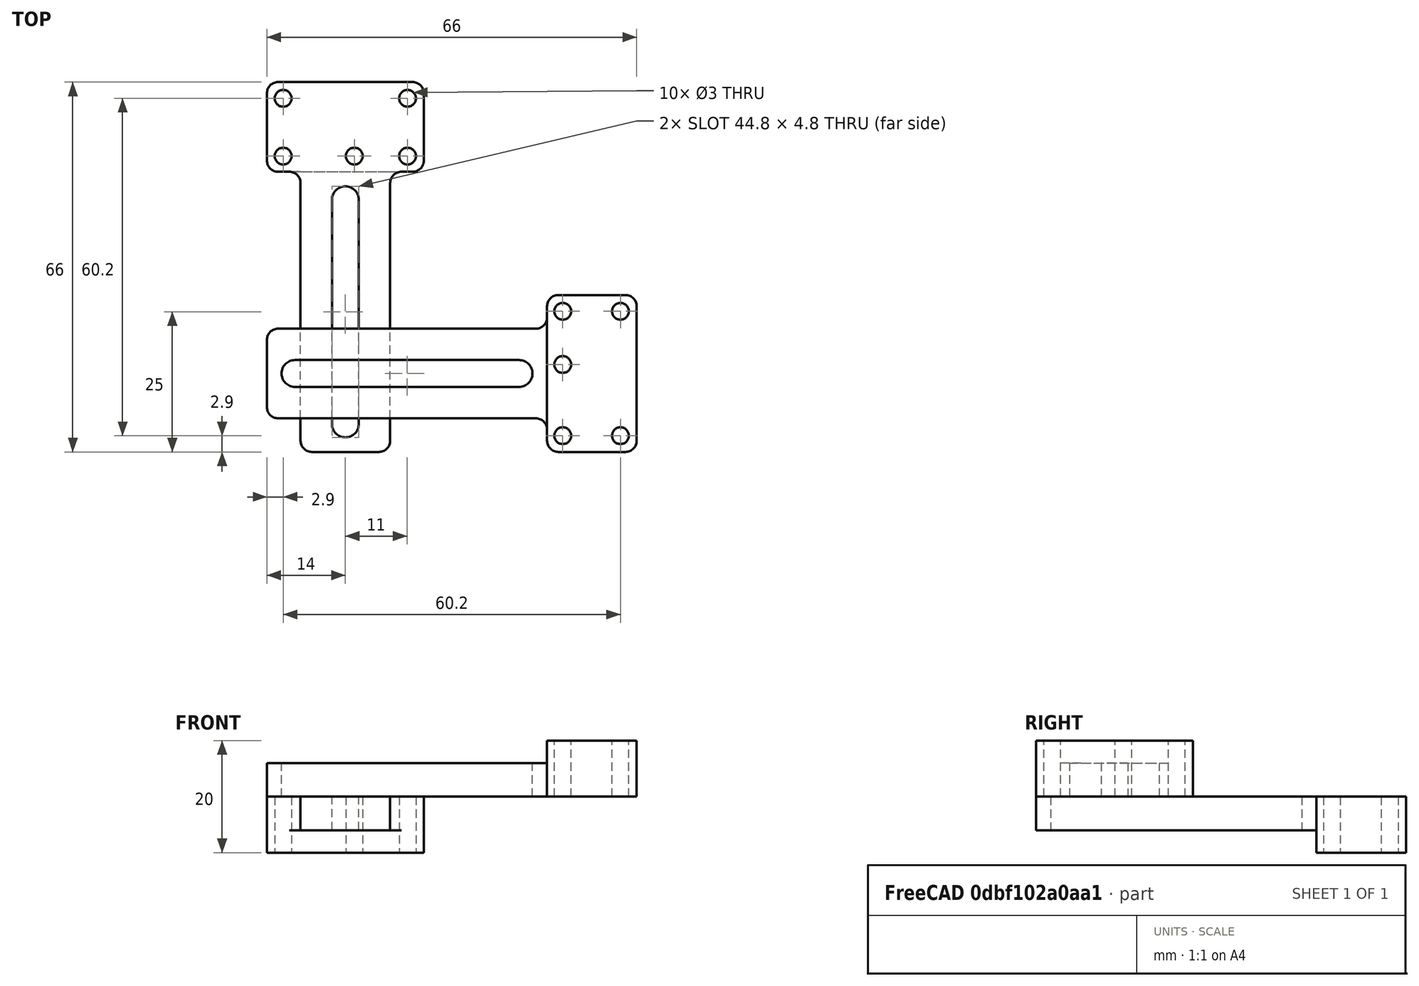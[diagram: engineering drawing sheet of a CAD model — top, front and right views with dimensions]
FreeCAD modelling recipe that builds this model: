
FCSTD DOCUMENT  (FreeCAD 0.15R4527 (Git))
Label: y_endstop_holder
License: All rights reserved
LicenseURL: http://en.wikipedia.org/wiki/All_rights_reserved
objects: Part::Cylinder×5, Part::Fillet×3, Part::Feature×2, Part::Box×2, Part::MultiFuse×2, Mesh::Feature×1, Sketcher::SketchObject×1, PartDesign::Pocket×1, Part::Cut×1
note: 18 computed .brp shape members not serialized (recipe doc carries the construction recipe); baked Part::Feature solids carry a one-line shape summary decoded from their .brp

FEATURE [Mesh::Feature] yendstopholder
FEATURE [Part::Feature] yendstopholder001001  label="yendstopholder002"
  shape: bbox 65.9 x 28 x 9.85 mm, 928 faces, 0 solids (baked)
FEATURE [Part::Box] Box  label="Cubo"
  Height = 6
  Length = 50
  Placement = pos=(0,6,0) rot=(0,0,1;0rad)
  Width = 16
FEATURE [Part::Box] Box001  label="Cubo001"
  Height = 10
  Length = 16
  Placement = pos=(50,0,0) rot=(0,0,1;0rad)
  Width = 28
FEATURE [Part::Fillet] Fillet
  Base = -> Box
  Edges = 2 edges r=2: [Edge1,Edge3]
FEATURE [Part::Fillet] Fillet001
  Base = -> Box001
  Edges = 4 edges r=2: [Edge1,Edge3,Edge5,Edge7]
FEATURE [Part::MultiFuse] Fusion
  Shapes = -> [Fillet,Fillet001]
FEATURE [Part::Fillet] Fillet002
  Base = -> Fusion
  Edges = 2 edges r=2: [Edge17,Edge18]
FEATURE [Sketcher::SketchObject] Sketch
  ExternalGeometry = -> [Fillet002]
  Placement = pos=(0,0,6) rot=(0,0,1;0rad)
  Support = -> Fillet002 [Face1]
  sketch-geometry (8):
    g0: ArcOfCircle CenterX=5 CenterY=14 CenterZ=0 NormalX=0 NormalY=0 NormalZ=1 Radius=2.4 StartAngle=1.5708 EndAngle=4.71239
    g1: ArcOfCircle CenterX=45 CenterY=14 CenterZ=0 NormalX=0 NormalY=0 NormalZ=1 Radius=2.4 StartAngle=4.71239 EndAngle=7.85398
    g2: LineSegment StartX=5 StartY=11.6 StartZ=0 EndX=45 EndY=11.6 EndZ=0
    g3: LineSegment StartX=5 StartY=16.4 StartZ=0 EndX=45 EndY=16.4 EndZ=0
    g4: LineSegment [constr] StartX=5 StartY=16.4 StartZ=0 EndX=5 EndY=22 EndZ=0
    g5: LineSegment [constr] StartX=5 StartY=11.6 StartZ=0 EndX=5 EndY=6 EndZ=0
    g6: LineSegment [constr] StartX=5 StartY=16.4 StartZ=0 EndX=0 EndY=16.4 EndZ=0
    g7: LineSegment [constr] StartX=45 StartY=16.4 StartZ=0 EndX=50 EndY=16.4 EndZ=0
  constraints (22):
    c: Tangent(g0,g3) = 1.5708
    c: Tangent(g0,g2) = -1.5708
    c: Tangent(g2,g1) = -1.5708
    c: Tangent(g3,g1) = 1.5708
    c: Horizontal(g2)
    c: Equal(g0,g1)
    c: Radius(g0) = 2.4
    c: Coincident(g4,g0)
    c: PointOnObject(g4,g-3)
    c: Vertical(g4)
    c: Coincident(g5,g0)
    c: PointOnObject(g5,g-4)
    c: Vertical(g5)
    c: Equal(g5,g4)
    c: DistanceX(g2) = 40
    c: Coincident(g6,g0)
    c: PointOnObject(g6,g-6)
    c: Horizontal(g6)
    c: Coincident(g7,g1)
    c: PointOnObject(g7,g-5)
    c: Horizontal(g7)
    c: Equal(g6,g7)
FEATURE [PartDesign::Pocket] Pocket
  Length = 5
  Sketch = -> Sketch
  Type = 1
FEATURE [Part::Cylinder] Cylinder  label="Cilindro"
  Angle = 360
  Height = 10
  Placement = pos=(52.8,2.9,0) rot=(0,0,1;0rad)
  Radius = 1.5
FEATURE [Part::Cylinder] Cylinder001  label="Cilindro001"
  Angle = 360
  Height = 10
  Placement = pos=(63.1,2.9,0) rot=(0,0,1;0rad)
  Radius = 1.5
FEATURE [Part::Cylinder] Cylinder002  label="Cilindro002"
  Angle = 360
  Height = 10
  Placement = pos=(52.8,15.6,0) rot=(0,0,1;0rad)
  Radius = 1.5
FEATURE [Part::Cylinder] Cylinder003  label="Cilindro003"
  Angle = 360
  Height = 10
  Placement = pos=(52.8,25.1,0) rot=(0,0,1;0rad)
  Radius = 1.5
FEATURE [Part::Cylinder] Cylinder004  label="Cilindro004"
  Angle = 360
  Height = 10
  Placement = pos=(63.1,25.1,0) rot=(0,0,1;0rad)
  Radius = 1.5
FEATURE [Part::MultiFuse] Fusion001
  Shapes = -> [Cylinder,Cylinder002,Cylinder003,Cylinder001,Cylinder004]
FEATURE [Part::Cut] Cut  label="y_endstop_holder"
  Base = -> Pocket
  Tool = -> Fusion001
FEATURE [Part::Feature] Cut001  label="y_endstop_holder001"
  Placement = pos=(0,0,0) rot=(0.707107,0.707107,0;3.14159rad)
  shape: bbox 28 x 66 x 10 mm, 27 faces (baked)
